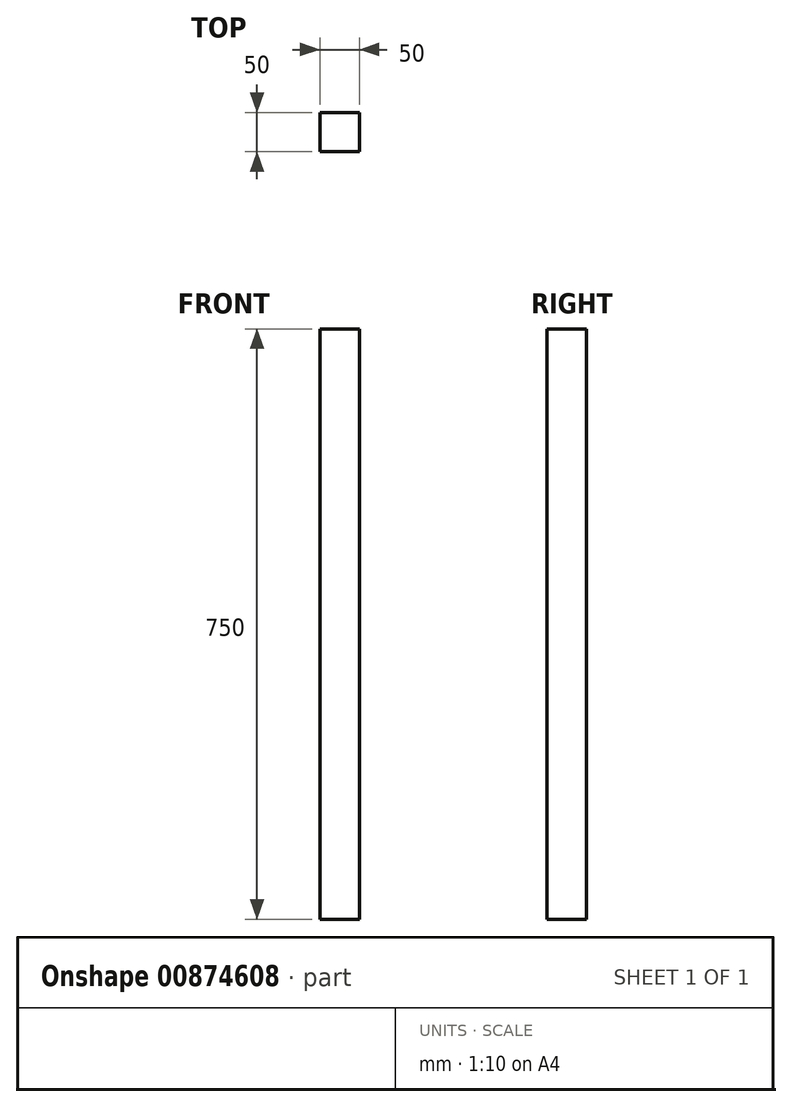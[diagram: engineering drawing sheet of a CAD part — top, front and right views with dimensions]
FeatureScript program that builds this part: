
annotation { "Feature Type Name" : "Feature", "Feature Type Description" : "" }
export const myFeature = defineFeature(function(context is Context, id is Id, definition is map)
    precondition{}
    {
        {
            var Q0;
            Q0=qCreatedBy(makeId("Top.planeOp"),FACE);
            var sketch = newSketch(context, id + "F0", { "sketchPlane" : qUnion([Q0])});
            skLineSegment(sketch, "E0.bottom", {"start": v(0, 0) * mm, "end": v(50, 0) * mm});
            skLineSegment(sketch, "E0.top", {"start": v(0, 50) * mm, "end": v(50, 50) * mm});
            skLineSegment(sketch, "E0.left", {"start": v(0, 0) * mm, "end": v(0, 50) * mm});
            skLineSegment(sketch, "E0.right", {"start": v(50, 0) * mm, "end": v(50, 50) * mm});
            skSolve(sketch);
        }
        {
            var Q0;
            Q0=makeQuery(id+"F0.imprint","IMPRINT",FACE,{"disambiguationData":[TD([[makeQuery(id+"F0.imprint","IMPRINT",EDGE,{"derivedFrom":sQuery(id+"F0.wireOp",EDGE,"E0.bottom")}),1.0]])]});
            extrude(context, id + "F1", {"entities" : qUnion([Q0]), "depth" : 750 * mm, "offsetDistance" : 25 * mm});
        }
    });
